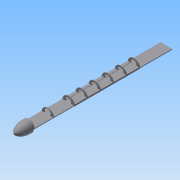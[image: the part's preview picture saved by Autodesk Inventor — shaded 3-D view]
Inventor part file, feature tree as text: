
AUTODESK INVENTOR PART (.ipt)
format: ipt  version: 2014 SP1 (Build 180222100, 222)  size: 246,272 bytes
history: native  units: mm
features: extrude x6, projected_geometry x6, sketch x5, pattern_linear x2, plane x2, revolve x1
ambient origin geometry x8: Origin, YZ Plane, XZ Plane, XY Plane, X Axis, Y Axis, Z Axis, Center Point
bodies: Solid1 (feature_tree)
feature tree (22):
  sketch  "Sketch1"  dims[d0=955.0mm d1=80.0mm]
  extrude  "Extrusion1"  Depth=80.0mm
  extrude  "Extrusion2"  Depth=20.0mm
  extrude  "Extrusion4"  Depth=150.0mm
  pattern_linear  "Rectangular Pattern1"  Count1=15  [1 undecoded]
  plane  "Work Plane1"
  sketch  "Sketch4"  dims[d4=456.0mm d5=150.0mm d6=150.0mm]
  extrude  "Extrusion5"  Depth=10.0mm TaperAngle=0.0deg
  extrude  "Extrusion6"  Depth=20.0mm
  extrude  "Extrusion7"  Depth=5.0mm TaperAngle=0.0deg
  pattern_linear  "Rectangular Pattern2"  Count1=2 Spacing1=133.5mm
  plane  "Work Plane2"
  revolve  "Revolution1"  [1 undecoded]
  sketch  "Sketch3"  dims[d2=277.0mm d3=20.0mm]
  projected_geometry  "Projected Loop1"
  projected_geometry  "Projected Loop2"
  projected_geometry  "Projected Loop3"
  projected_geometry  "Projected Loop4"
  projected_geometry  "Projected Loop5"
  projected_geometry  "Projected Loop6"
  sketch  "Sketch5"  dims[d7=5.0mm d8=0.0mm d9=10.0mm d10=0.0mm]
  sketch  "Sketch6"  dims[d18=20.0mm d19=20.0mm d20=5.0mm d21=0.0mm d22=20.0mm d24=133.5mm d25=277.0mm d26=80.0mm d27=5.0mm d28=0.0mm d29=500.0mm d30=0.0mm d33=5.0mm d34=5.0mm d35=500.0mm d36=0.0mm d37=60.0mm d39=90.2mm d40=40.0mm d41=100.0mm d42=48.869219mm]
note: 2 required parameter values undecoded (feature->parameter linkage not recoverable at this tier; creation-order binding heuristic only, values carry confidence <= 0.55)